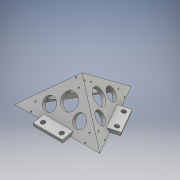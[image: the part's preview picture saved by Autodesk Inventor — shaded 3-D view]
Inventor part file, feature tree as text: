
AUTODESK INVENTOR PART (.ipt)
format: ipt  version: 2016 (Build 200138000, 138)  size: 265,216 bytes
history: native  units: mm
features: sketch x7, plane x4, extrude x4, pattern_circular x4, hole x2, other x1, projected_geometry x1
ambient origin geometry x8: Origin, YZ Plane, XZ Plane, XY Plane, X Axis, Y Axis, Z Axis, Center Point
bodies: Solid1 (feature_tree)
feature tree (23):
  sketch  "Sketch1"  dims[d0=82.0mm d1=82.0mm]
  other  "Work Axis1"
  sketch  "Sketch2"  dims[d2=82.0mm]
  plane  "Work Plane2"
  extrude  "Extrusion1"  Depth=82.0mm
  pattern_circular  "Circular Pattern1"  Count=3 Angle=360.0deg
  sketch  "Sketch4"  dims[d4=3.0mm d5=-7.853982mm d6=30.0mm d7=360.0deg]
  hole  "Hole2"  [1 undecoded]
  pattern_circular  "Circular Pattern2"  Count=3 Angle=360.0deg
  extrude  "Extrusion3"  Depth=2.0mm
  extrude  "Extrusion2"  Depth=2.0mm
  pattern_circular  "Circular Pattern4"  [2 undecoded]
  plane  "Work Plane4"
  extrude  "Extrusion4"  Depth=5.0mm TaperAngle=0.0deg
  hole  "Hole3"  [1 undecoded]
  pattern_circular  "Circular Pattern5"  [2 undecoded]
  plane  "Work Plane1"
  sketch  "Sketch3"  dims[d3=35.0mm]
  projected_geometry  "Projected Loop1"
  sketch  "Sketch5"  dims[d10=7.62mm d11=1.27mm]
  sketch  "Sketch7"  dims[d19=1.181mm d20=3.048mm d21=4.0mm d22=2.0mm d23=90.0deg d24=4.636mm d25=20.594885mm d26=30.0mm d27=360.0deg]
  plane  "Work Plane3"
  sketch  "Sketch9"  dims[d29=7.62mm d30=15.0mm d31=12.0mm d32=12.0mm d33=5.0mm d34=0.0mm d42=12.0mm d43=28.0mm d44=4.0mm d45=4.0mm d46=5.0mm d47=5.0mm d48=3.0mm d49=0.0mm d50=2.5mm d51=0.0mm d52=30.0mm d53=360.0deg d55=23.0mm d56=10.0mm d57=0.0mm d58=10.16mm d59=5.08mm d60=1.27mm d61=10.16mm d62=10.16mm d63=10.16mm d64=5.08mm d65=1.27mm d66=1.181mm d67=3.048mm d68=4.0mm d69=2.0mm d70=90.0deg d71=4.636mm d72=20.594885mm d73=30.0mm d74=360.0deg]
note: 6 required parameter values undecoded (feature->parameter linkage not recoverable at this tier; creation-order binding heuristic only, values carry confidence <= 0.55)
